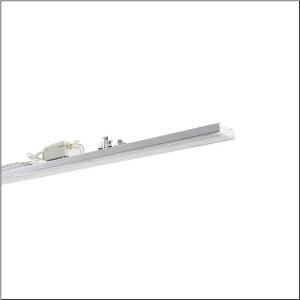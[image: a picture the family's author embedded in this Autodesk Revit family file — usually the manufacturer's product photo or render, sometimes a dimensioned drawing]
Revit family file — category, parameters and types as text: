
# Revit family: licross_21_recessed_ho_52tl12dn4fxm3c
name_source: partatom
category: Lighting Fixtures
units: mm (PartAtom-declared; Revit-internal decimal feet)

## family parameters
Cut with Voids When Loaded = No
Host = Face
Light Source = No
Part Type = Normal
Room Calculation Point = No
Round Connector Dimension = Use Diameter
Shared = No

## types (1)
- --- (1 x LED, 930 lm, 7.5 W, 4000K)
    Apparent Load = 8 VA
    CIE Flux Codes = 69 91 98 100 100
    Color Rendering = 80
    Color Temperature = 4000K
    Default Elevation = 1800 mm
    Description = Licross 21 Recessed HO, luminaire insert, of sheet steel, galvanised, coil coated, white, length: 1.500mm, width: 66mm, height: 67mm, LED rated luminous flux: 15.000lm, light colour: 840, SDCM (Standard Deviation of Colour Matching)MacAdam ≤ 3 SDCM (initial), control gear: DALI 2 (for two DALI lines), with plug, 6-pole, with phase selection, for trunking rail, 14-core, mains connection: 220..240V, AC, 50/60Hz, rated input power: 88W, internal wiring halogen-free, for emergency light function, for trunking rail, 14-core, converter,control gear: single battery element, battery: LiFePO4, 9Ah, primary optical cover: cover, of PMMA, light emission: direct distribution, primary light characteristic: symmetric, protection rating (complete): IP40, insulation class (complete): insulation class I (protective earthing), certification: CE, UKCA, protection symbol: D if used in an environment without relevant dust loads with corresponding accessories, impact resistance: IK06, permissible ambient temperature for indoor applications: +5..+30°C, standard: EN 60598-2-22, LABS conformity tested according to VDMA 24364:2018-05, reducing of maximum allowable ambient temperature of 5°C with ceiling mounting, corresponds to IFS (International Featured Standards) requirements for safety and quality in the food industry, The light source and the operating device comply with the requirements of the Ecodesign Regulation (EU) 2019/2020 and are replaceable in accordance with this regulation, packaging unit: 1 piece
    Height = 58 mm
    Lamp = 1 x LED
    Lamp Light Flux = 930 lm
    Lamp Power = 7.5 W
    Lamp count = 1
    Length = 1500 mm
    Luminous efficacy = 124 lm/W
    Manufacturer = Siteco
    ModVariant = No
    Model = 52TL12DN4FXM3C
    Mounting Place = Ceiling
    Mounting Type = Pendant
    Number of Poles = 1
    OnlyDefault = Yes
    Power Factor = 1
    Product Name = Licross 21 Recessed HO
    Product group = luminaire insert | ceiling pendant
    ProductGroupID = 901
    Protection Class = Protection class I
    Protection Degree = IP 40
    RLX_Detail_Level = 1
    RLX_Emergency_Light_Flux = 0 lm
    RLX_Emergency_Type = 0
    RLX_Emergency_Type_DB = No
    RlxData = <blob elided: 25373 chars, md5=7b3f4512>
    Socket = socket
    Standby Power = 0 W
    System Light Flux = 930 lm
    System Power = 8 W
    Type Comments = : emergency light operation: 3 h
    Type Image = l_1296930.jpg
    URL = http://relux.com
    VarID = @adj_110779
    Voltage = 0 V
    Weight = 0.00 kg
    Width = 66 mm

## geometry (parser evidence)
native form markers: Blend x4, Sweep x11
no freeform markers — native parametric forms only
